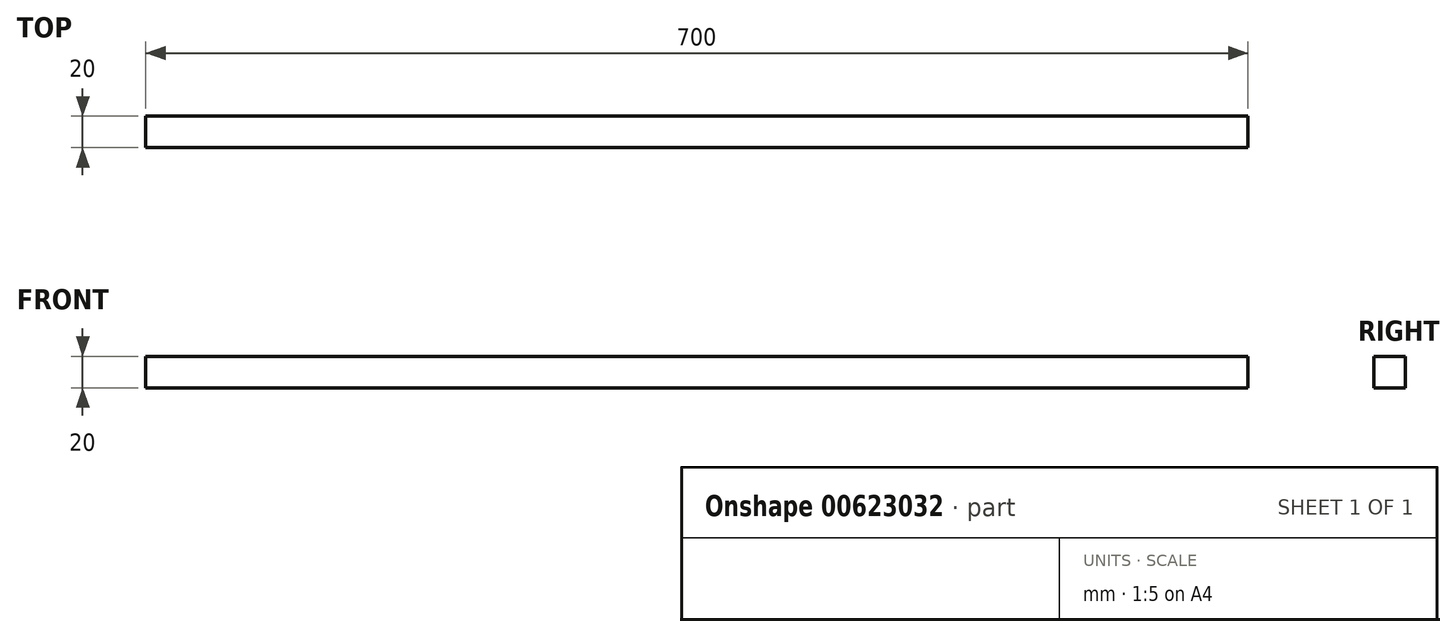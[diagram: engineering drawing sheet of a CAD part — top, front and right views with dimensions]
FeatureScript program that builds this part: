
annotation { "Feature Type Name" : "Feature", "Feature Type Description" : "" }
export const myFeature = defineFeature(function(context is Context, id is Id, definition is map)
    precondition{}
    {
        {
            var Q0;
            Q0=qCreatedBy(makeId("Top.planeOp"),FACE);
            var sketch = newSketch(context, id + "F0", { "sketchPlane" : qUnion([Q0])});
            skLineSegment(sketch, "E0.bottom", {"start": v(0, 0) * mm, "end": v(700, 0) * mm});
            skLineSegment(sketch, "E0.top", {"start": v(0, 20) * mm, "end": v(700, 20) * mm});
            skLineSegment(sketch, "E0.left", {"start": v(0, 0) * mm, "end": v(0, 20) * mm});
            skLineSegment(sketch, "E0.right", {"start": v(700, 0) * mm, "end": v(700, 20) * mm});
            skSolve(sketch);
        }
        {
            var Q0;
            Q0 = qSketchRegion(id + "F0", true);
            extrude(context, id + "F1", {"entities" : qUnion([Q0]), "depth" : 20 * mm, "offsetDistance" : 25 * mm});
        }
    });
